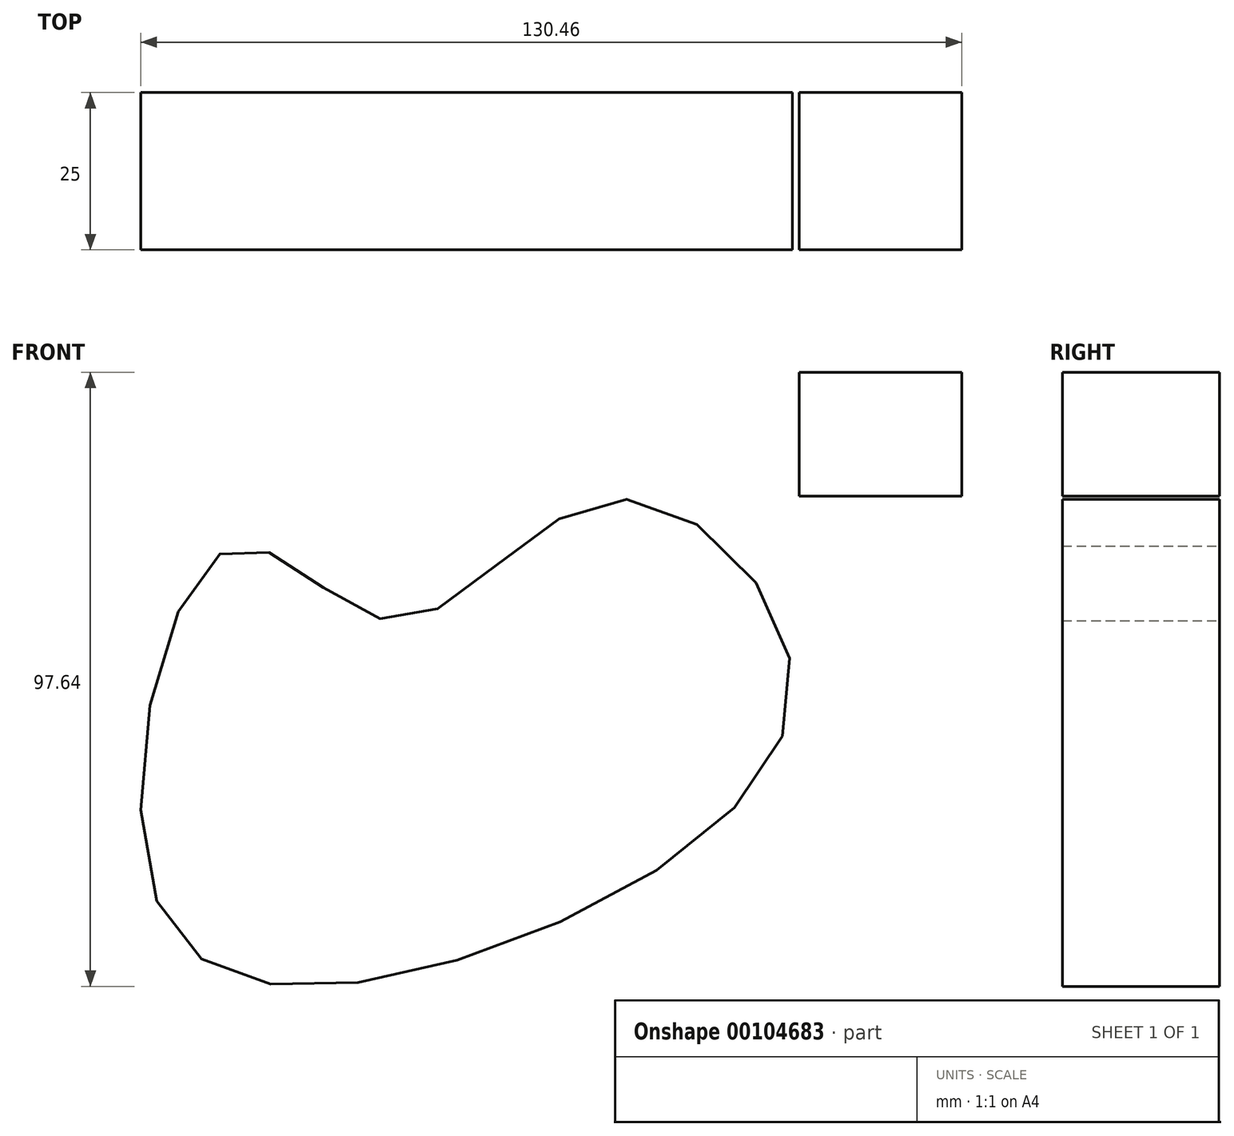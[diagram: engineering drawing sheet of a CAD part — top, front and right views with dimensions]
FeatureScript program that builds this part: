
annotation { "Feature Type Name" : "Feature", "Feature Type Description" : "" }
export const myFeature = defineFeature(function(context is Context, id is Id, definition is map)
    precondition{}
    {
        {
            var Q0;
            Q0=qCreatedBy(makeId("Front.planeOp"),FACE);
            var sketch = newSketch(context, id + "F0", { "sketchPlane" : qUnion([Q0])});
            skFitSpline(sketch, "E0", {"points": [v(-82.59, -21.63) * mm, v(-70.6, 34.55) * mm, v(-44.76, 22.94) * mm, v(-10.11, 42.23) * mm, v(18.35, 11.33) * mm, v(-38.02, -31.93) * mm, v(-82.59, -21.63) * mm]});
            skLineSegment(sketch, "E1.bottom", {"start": v(19.48, 62.46) * mm, "end": v(45.32, 62.46) * mm});
            skLineSegment(sketch, "E1.top", {"start": v(19.48, 42.8) * mm, "end": v(45.32, 42.8) * mm});
            skLineSegment(sketch, "E1.left", {"start": v(19.48, 62.46) * mm, "end": v(19.48, 42.8) * mm});
            skLineSegment(sketch, "E1.right", {"start": v(45.32, 62.46) * mm, "end": v(45.32, 42.8) * mm});
            skSolve(sketch);
        }
        {
            var Q0;
            Q0 = qSketchRegion(id + "F0", true);
            extrude(context, id + "F1", {"entities" : qUnion([Q0]), "depth" : 25 * mm});
        }
    });
